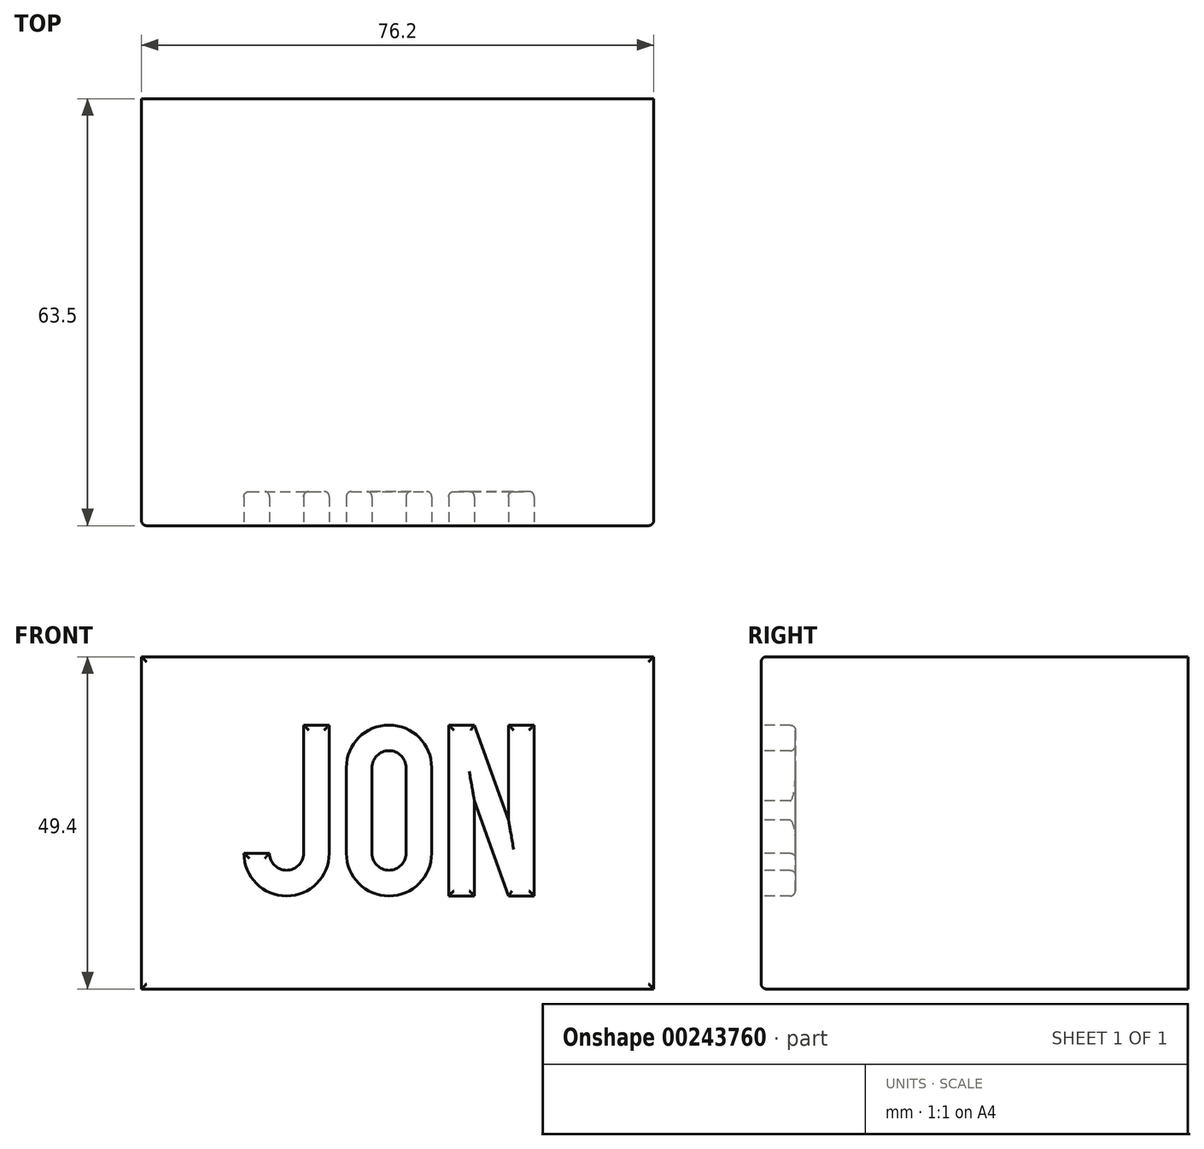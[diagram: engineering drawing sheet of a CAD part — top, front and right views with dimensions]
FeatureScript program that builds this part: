
annotation { "Feature Type Name" : "Feature", "Feature Type Description" : "" }
export const myFeature = defineFeature(function(context is Context, id is Id, definition is map)
    precondition{}
    {
        {
            var Q0;
            Q0=qCreatedBy(makeId("Front.planeOp"),FACE);
            var sketch = newSketch(context, id + "F0", { "sketchPlane" : qUnion([Q0])});
            skLineSegment(sketch, "E0.bottom", {"start": v(0, -49.4) * mm, "end": v(76.2, -49.4) * mm});
            skLineSegment(sketch, "E0.top", {"start": v(0, 0) * mm, "end": v(76.2, 0) * mm});
            skLineSegment(sketch, "E0.left", {"start": v(0, -49.4) * mm, "end": v(0, 0) * mm});
            skLineSegment(sketch, "E0.right", {"start": v(76.2, -49.4) * mm, "end": v(76.2, 0) * mm});
            skSolve(sketch);
        }
        {
            var Q0;
            Q0=makeQuery(id+"F0.imprint","IMPRINT",FACE,{"disambiguationData":[TD([[makeQuery(id+"F0.imprint","IMPRINT",EDGE,{"derivedFrom":sQuery(id+"F0.wireOp",EDGE,"E0.bottom")}),1.0]])]});
            extrude(context, id + "F1", {"entities" : qUnion([Q0]), "depth" : 63.5 * mm});
        }
        {
            var Q0;
            Q0=makeQuery(id+"F1.opExtrude","CAP_FACE",FACE,{"disambiguationData":[OSD([sQuery(id+"F0.wireOp",EDGE,"E0.bottom"),sQuery(id+"F0.wireOp",EDGE,"E0.top"),sQuery(id+"F0.wireOp",EDGE,"E0.left"),sQuery(id+"F0.wireOp",EDGE,"E0.right")])],"isStart":false});
            var sketch = newSketch(context, id + "F2", { "sketchPlane" : qUnion([Q0])});
            skLineSegment(sketch, "E1", {"start": v(24.13, -10.16) * mm, "end": v(27.94, -10.16) * mm});
            skLineSegment(sketch, "E2", {"start": v(27.94, -10.16) * mm, "end": v(27.94, -29.2) * mm});
            skLineSegment(sketch, "E3", {"start": v(24.13, -10.16) * mm, "end": v(24.13, -29.2) * mm});
            skLineSegment(sketch, "E4", {"start": v(45.72, -35.56) * mm, "end": v(45.72, -10.16) * mm});
            skLineSegment(sketch, "E5", {"start": v(45.72, -10.16) * mm, "end": v(49.53, -10.16) * mm});
            skLineSegment(sketch, "E6", {"start": v(49.53, -10.16) * mm, "end": v(54.61, -24.3) * mm});
            skLineSegment(sketch, "E7", {"start": v(54.61, -24.3) * mm, "end": v(54.61, -10.16) * mm});
            skLineSegment(sketch, "E8", {"start": v(54.61, -10.16) * mm, "end": v(58.42, -10.16) * mm});
            skLineSegment(sketch, "E9", {"start": v(58.42, -10.16) * mm, "end": v(58.42, -35.56) * mm});
            skLineSegment(sketch, "E10", {"start": v(58.42, -35.56) * mm, "end": v(54.61, -35.56) * mm});
            skLineSegment(sketch, "E11", {"start": v(54.61, -35.56) * mm, "end": v(49.53, -21.43) * mm});
            skLineSegment(sketch, "E12", {"start": v(49.53, -21.43) * mm, "end": v(49.53, -35.56) * mm});
            skLineSegment(sketch, "E13", {"start": v(49.53, -35.56) * mm, "end": v(45.72, -35.56) * mm});
            skArc(sketch, "E14", {"start": v(15.24, -29.2) * mm, "mid": v(21.6, -35.56) * mm, "end": v(27.94, -29.2) * mm});
            skArc(sketch, "E15", {"start": v(19.05, -29.2) * mm, "mid": v(21.59, -31.75) * mm, "end": v(24.13, -29.2) * mm});
            skArc(sketch, "E16", {"start": v(39.37, -16.5) * mm, "mid": v(36.83, -13.97) * mm, "end": v(34.29, -16.5) * mm});
            skArc(sketch, "E17", {"start": v(34.3, -29.2) * mm, "mid": v(36.83, -31.75) * mm, "end": v(39.37, -29.2) * mm});
            skArc(sketch, "E18", {"start": v(43.18, -16.5) * mm, "mid": v(36.83, -10.16) * mm, "end": v(30.48, -16.5) * mm});
            skArc(sketch, "E19", {"start": v(30.48, -29.2) * mm, "mid": v(36.83, -35.56) * mm, "end": v(43.18, -29.2) * mm});
            skLineSegment(sketch, "E20", {"start": v(30.48, -16.5) * mm, "end": v(30.48, -29.2) * mm});
            skLineSegment(sketch, "E21", {"start": v(43.18, -16.5) * mm, "end": v(43.18, -29.2) * mm});
            skLineSegment(sketch, "E22", {"start": v(39.37, -16.5) * mm, "end": v(39.37, -29.2) * mm});
            skLineSegment(sketch, "E23", {"start": v(34.3, -16.5) * mm, "end": v(34.3, -29.2) * mm});
            skLineSegment(sketch, "E24", {"start": v(15.24, -29.21) * mm, "end": v(19.05, -29.2) * mm});
            skSolve(sketch);
        }
        {
            var Q0;
            Q0=makeQuery(id+"F2.imprint","IMPRINT",FACE,{"disambiguationData":[TD([[makeQuery(id+"F2.imprint","IMPRINT",EDGE,{"derivedFrom":sQuery(id+"F2.wireOp",EDGE,"E1")}),-1.0]])]});
            var Q1;
            Q1=makeQuery(id+"F2.imprint","IMPRINT",FACE,{"disambiguationData":[TD([[makeQuery(id+"F2.imprint","IMPRINT",EDGE,{"derivedFrom":sQuery(id+"F2.wireOp",EDGE,"E16")}),-1.0]])]});
            var Q2;
            Q2=makeQuery(id+"F2.imprint","IMPRINT",FACE,{"disambiguationData":[TD([[makeQuery(id+"F2.imprint","IMPRINT",EDGE,{"derivedFrom":sQuery(id+"F2.wireOp",EDGE,"E4")}),-1.0]])]});
            extrude(context, id + "F3", {"entities" : qUnion([Q0, Q1, Q2]), "operationType" : NewBodyOperationType.REMOVE, "oppositeDirection" : true, "depth" : 5.08 * mm});
        }
        {
            var Q0;
            Q0=makeQuery(id+"F1.opExtrude","CAP_EDGE",EDGE,{"disambiguationData":[OSD([sQuery(id+"F0.wireOp",EDGE,"E0.top")])],"isStart":false});
            var Q1;
            Q1=makeQuery(id+"F1.opExtrude","CAP_EDGE",EDGE,{"disambiguationData":[OSD([sQuery(id+"F0.wireOp",EDGE,"E0.left")])],"isStart":false});
            var Q2;
            Q2=makeQuery(id+"F1.opExtrude","CAP_EDGE",EDGE,{"disambiguationData":[OSD([sQuery(id+"F0.wireOp",EDGE,"E0.bottom")])],"isStart":false});
            var Q3;
            Q3=makeQuery(id+"F1.opExtrude","CAP_EDGE",EDGE,{"disambiguationData":[OSD([sQuery(id+"F0.wireOp",EDGE,"E0.right")])],"isStart":false});
            var Q4;
            Q4=makeQuery(id+"F3.boolean.opBoolean","COPY",EDGE,{"derivedFrom":makeQuery(id+"F3.opExtrude","CAP_EDGE",EDGE,{"disambiguationData":[OSD([sQuery(id+"F2.wireOp",EDGE,"E9")])],"isStart":true})});
            var Q5;
            Q5=makeQuery(id+"F3.boolean.opBoolean","COPY",EDGE,{"derivedFrom":makeQuery(id+"F3.opExtrude","CAP_EDGE",EDGE,{"disambiguationData":[OSD([sQuery(id+"F2.wireOp",EDGE,"E8")])],"isStart":true})});
            var Q6;
            Q6=makeQuery(id+"F3.boolean.opBoolean","COPY",EDGE,{"derivedFrom":makeQuery(id+"F3.opExtrude","CAP_EDGE",EDGE,{"disambiguationData":[OSD([sQuery(id+"F2.wireOp",EDGE,"E7")])],"isStart":true})});
            var Q7;
            Q7=makeQuery(id+"F3.boolean.opBoolean","COPY",EDGE,{"derivedFrom":makeQuery(id+"F3.opExtrude","CAP_EDGE",EDGE,{"disambiguationData":[OSD([sQuery(id+"F2.wireOp",EDGE,"E6")])],"isStart":true})});
            var Q8;
            Q8=makeQuery(id+"F3.boolean.opBoolean","COPY",EDGE,{"derivedFrom":makeQuery(id+"F3.opExtrude","CAP_EDGE",EDGE,{"disambiguationData":[OSD([sQuery(id+"F2.wireOp",EDGE,"E5")])],"isStart":true})});
            var Q9;
            Q9=makeQuery(id+"F3.boolean.opBoolean","COPY",EDGE,{"derivedFrom":makeQuery(id+"F3.opExtrude","CAP_EDGE",EDGE,{"disambiguationData":[OSD([sQuery(id+"F2.wireOp",EDGE,"E4")])],"isStart":true})});
            var Q10;
            Q10=makeQuery(id+"F3.boolean.opBoolean","COPY",EDGE,{"derivedFrom":makeQuery(id+"F3.opExtrude","CAP_EDGE",EDGE,{"disambiguationData":[OSD([sQuery(id+"F2.wireOp",EDGE,"E13")])],"isStart":true})});
            var Q11;
            Q11=makeQuery(id+"F3.boolean.opBoolean","COPY",EDGE,{"derivedFrom":makeQuery(id+"F3.opExtrude","CAP_EDGE",EDGE,{"disambiguationData":[OSD([sQuery(id+"F2.wireOp",EDGE,"E12")])],"isStart":true})});
            var Q12;
            Q12=makeQuery(id+"F3.boolean.opBoolean","COPY",EDGE,{"derivedFrom":makeQuery(id+"F3.opExtrude","CAP_EDGE",EDGE,{"disambiguationData":[OSD([sQuery(id+"F2.wireOp",EDGE,"E11")])],"isStart":true})});
            var Q13;
            Q13=makeQuery(id+"F3.boolean.opBoolean","COPY",EDGE,{"derivedFrom":makeQuery(id+"F3.opExtrude","CAP_EDGE",EDGE,{"disambiguationData":[OSD([sQuery(id+"F2.wireOp",EDGE,"E10")])],"isStart":true})});
            var Q14;
            Q14=makeQuery(id+"F3.boolean.opBoolean","COPY",EDGE,{"derivedFrom":makeQuery(id+"F3.opExtrude","CAP_EDGE",EDGE,{"disambiguationData":[OSD([sQuery(id+"F2.wireOp",EDGE,"E21")])],"isStart":true})});
            var Q15;
            Q15=makeQuery(id+"F3.boolean.opBoolean","COPY",EDGE,{"derivedFrom":makeQuery(id+"F3.opExtrude","CAP_EDGE",EDGE,{"disambiguationData":[OSD([sQuery(id+"F2.wireOp",EDGE,"E18")])],"isStart":true})});
            var Q16;
            Q16=makeQuery(id+"F3.boolean.opBoolean","COPY",EDGE,{"derivedFrom":makeQuery(id+"F3.opExtrude","CAP_EDGE",EDGE,{"disambiguationData":[OSD([sQuery(id+"F2.wireOp",EDGE,"E20")])],"isStart":true})});
            var Q17;
            Q17=makeQuery(id+"F3.boolean.opBoolean","COPY",EDGE,{"derivedFrom":makeQuery(id+"F3.opExtrude","CAP_EDGE",EDGE,{"disambiguationData":[OSD([sQuery(id+"F2.wireOp",EDGE,"E19")])],"isStart":true})});
            var Q18;
            Q18=makeQuery(id+"F3.boolean.opBoolean","COPY",EDGE,{"derivedFrom":makeQuery(id+"F3.opExtrude","CAP_EDGE",EDGE,{"disambiguationData":[OSD([sQuery(id+"F2.wireOp",EDGE,"E2")])],"isStart":true})});
            var Q19;
            Q19=makeQuery(id+"F3.boolean.opBoolean","COPY",EDGE,{"derivedFrom":makeQuery(id+"F3.opExtrude","CAP_EDGE",EDGE,{"disambiguationData":[OSD([sQuery(id+"F2.wireOp",EDGE,"E1")])],"isStart":true})});
            var Q20;
            Q20=makeQuery(id+"F3.boolean.opBoolean","COPY",EDGE,{"derivedFrom":makeQuery(id+"F3.opExtrude","CAP_EDGE",EDGE,{"disambiguationData":[OSD([sQuery(id+"F2.wireOp",EDGE,"E3")])],"isStart":true})});
            var Q21;
            Q21=makeQuery(id+"F3.boolean.opBoolean","COPY",EDGE,{"derivedFrom":makeQuery(id+"F3.opExtrude","CAP_EDGE",EDGE,{"disambiguationData":[OSD([sQuery(id+"F2.wireOp",EDGE,"E15")])],"isStart":true})});
            var Q22;
            Q22=makeQuery(id+"F3.boolean.opBoolean","COPY",EDGE,{"derivedFrom":makeQuery(id+"F3.opExtrude","CAP_EDGE",EDGE,{"disambiguationData":[OSD([sQuery(id+"F2.wireOp",EDGE,"E24")])],"isStart":true})});
            var Q23;
            Q23=makeQuery(id+"F3.boolean.opBoolean","COPY",EDGE,{"derivedFrom":makeQuery(id+"F3.opExtrude","CAP_EDGE",EDGE,{"disambiguationData":[OSD([sQuery(id+"F2.wireOp",EDGE,"E14")])],"isStart":true})});
            var Q24;
            Q24=makeQuery(id+"F3.boolean.opBoolean","COPY",FACE,{"derivedFrom":makeQuery(id+"F3.opExtrude","CAP_FACE",FACE,{"disambiguationData":[OSD([sQuery(id+"F2.wireOp",EDGE,"E16"),sQuery(id+"F2.wireOp",EDGE,"E17"),sQuery(id+"F2.wireOp",EDGE,"E18"),sQuery(id+"F2.wireOp",EDGE,"E19"),sQuery(id+"F2.wireOp",EDGE,"E20"),sQuery(id+"F2.wireOp",EDGE,"E21"),sQuery(id+"F2.wireOp",EDGE,"E22"),sQuery(id+"F2.wireOp",EDGE,"E23")])],"isStart":false})});
            var Q25;
            Q25=makeQuery(id+"F3.boolean.opBoolean","COPY",FACE,{"derivedFrom":makeQuery(id+"F3.opExtrude","CAP_FACE",FACE,{"disambiguationData":[OSD([sQuery(id+"F2.wireOp",EDGE,"E4"),sQuery(id+"F2.wireOp",EDGE,"E5"),sQuery(id+"F2.wireOp",EDGE,"E6"),sQuery(id+"F2.wireOp",EDGE,"E7"),sQuery(id+"F2.wireOp",EDGE,"E8"),sQuery(id+"F2.wireOp",EDGE,"E9"),sQuery(id+"F2.wireOp",EDGE,"E10"),sQuery(id+"F2.wireOp",EDGE,"E11"),sQuery(id+"F2.wireOp",EDGE,"E12"),sQuery(id+"F2.wireOp",EDGE,"E13")])],"isStart":false})});
            var Q26;
            Q26=makeQuery(id+"F3.boolean.opBoolean","COPY",FACE,{"derivedFrom":makeQuery(id+"F3.opExtrude","CAP_FACE",FACE,{"disambiguationData":[OSD([sQuery(id+"F2.wireOp",EDGE,"E1"),sQuery(id+"F2.wireOp",EDGE,"E2"),sQuery(id+"F2.wireOp",EDGE,"E3"),sQuery(id+"F2.wireOp",EDGE,"E14"),sQuery(id+"F2.wireOp",EDGE,"E15"),sQuery(id+"F2.wireOp",EDGE,"E24")])],"isStart":false})});
            fillet(context, id + "F4", {"entities" : qUnion([Q0, Q1, Q2, Q3, Q4, Q5, Q6, Q7, Q8, Q9, Q10, Q11, Q12, Q13, Q14, Q15, Q16, Q17, Q18, Q19, Q20, Q21, Q22, Q23, Q24, Q25, Q26]), "radius" : 0.76 * mm, "tangentPropagation" : true, "allowEdgeOverflow" : false});
        }
    });
